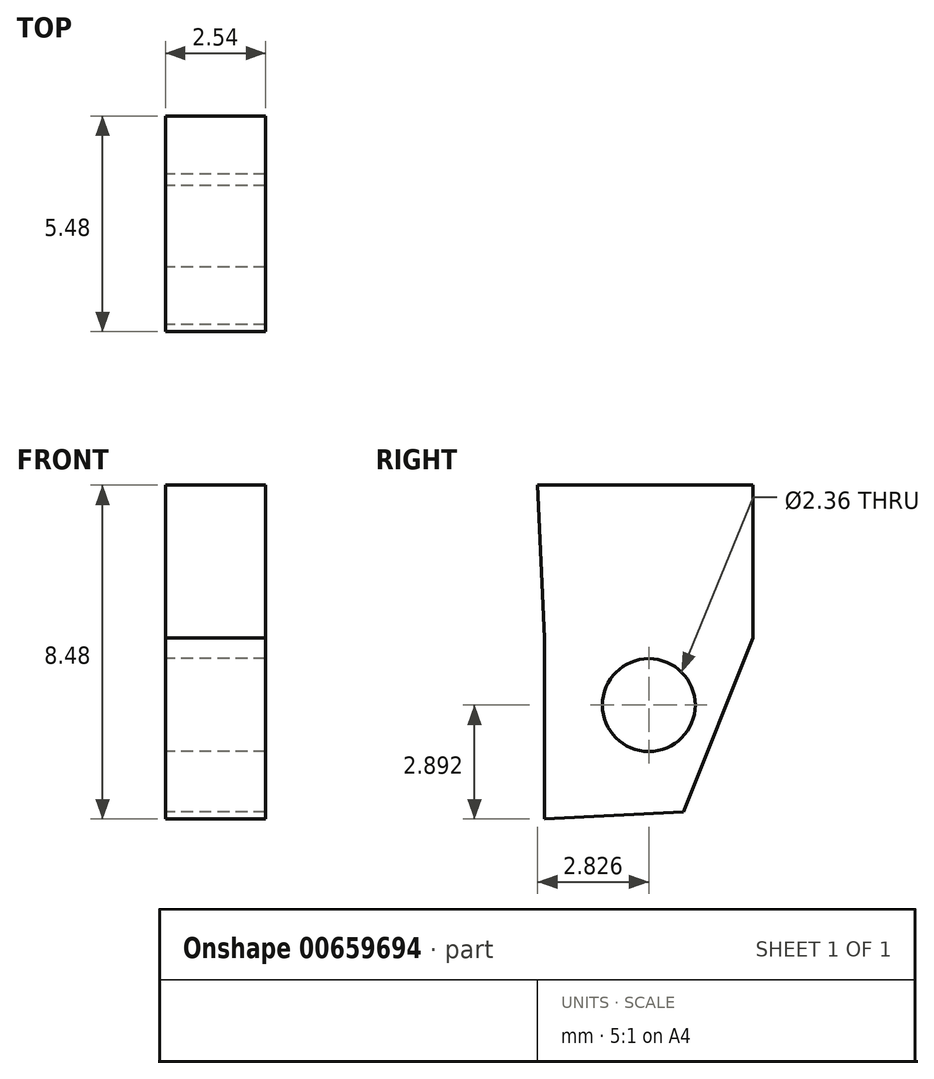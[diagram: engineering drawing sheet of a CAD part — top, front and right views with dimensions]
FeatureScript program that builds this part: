
annotation { "Feature Type Name" : "Feature", "Feature Type Description" : "" }
export const myFeature = defineFeature(function(context is Context, id is Id, definition is map)
    precondition{}
    {
        {
            var Q0;
            Q0=qCreatedBy(makeId("Right.planeOp"),FACE);
            var sketch = newSketch(context, id + "F0", { "sketchPlane" : qUnion([Q0])});
            skLineSegment(sketch, "E0", {"start": v(-2.61, 4.21) * mm, "end": v(2.87, 4.21) * mm});
            skLineSegment(sketch, "E1", {"start": v(2.87, 4.21) * mm, "end": v(2.87, 0.33) * mm});
            skLineSegment(sketch, "E2", {"start": v(2.87, 0.33) * mm, "end": v(-2.43, 0.33) * mm});
            skLineSegment(sketch, "E3", {"start": v(-2.43, 0.33) * mm, "end": v(-2.61, 4.21) * mm});
            skLineSegment(sketch, "E4", {"start": v(-2.43, 0.33) * mm, "end": v(-2.43, -4.27) * mm});
            skLineSegment(sketch, "E5", {"start": v(2.87, 0.33) * mm, "end": v(1.1, -4.09) * mm});
            skLineSegment(sketch, "E6", {"start": v(1.1, -4.09) * mm, "end": v(-2.43, -4.27) * mm});
            skCircle(sketch, "E7", {"center": v(0.22, -1.38) * mm, "radius": 1.18 * mm});
            skPoint(sketch, "E7.centerSnap0", {"position": v(0.22, 0.33) * mm});
            skSolve(sketch);
        }
        {
            var Q0;
            Q0 = qSketchRegion(id + "F0", true);
            extrude(context, id + "F1", {"entities" : qUnion([Q0]), "depth" : 2.54 * mm, "offsetDistance" : 25.4 * mm});
        }
    });
